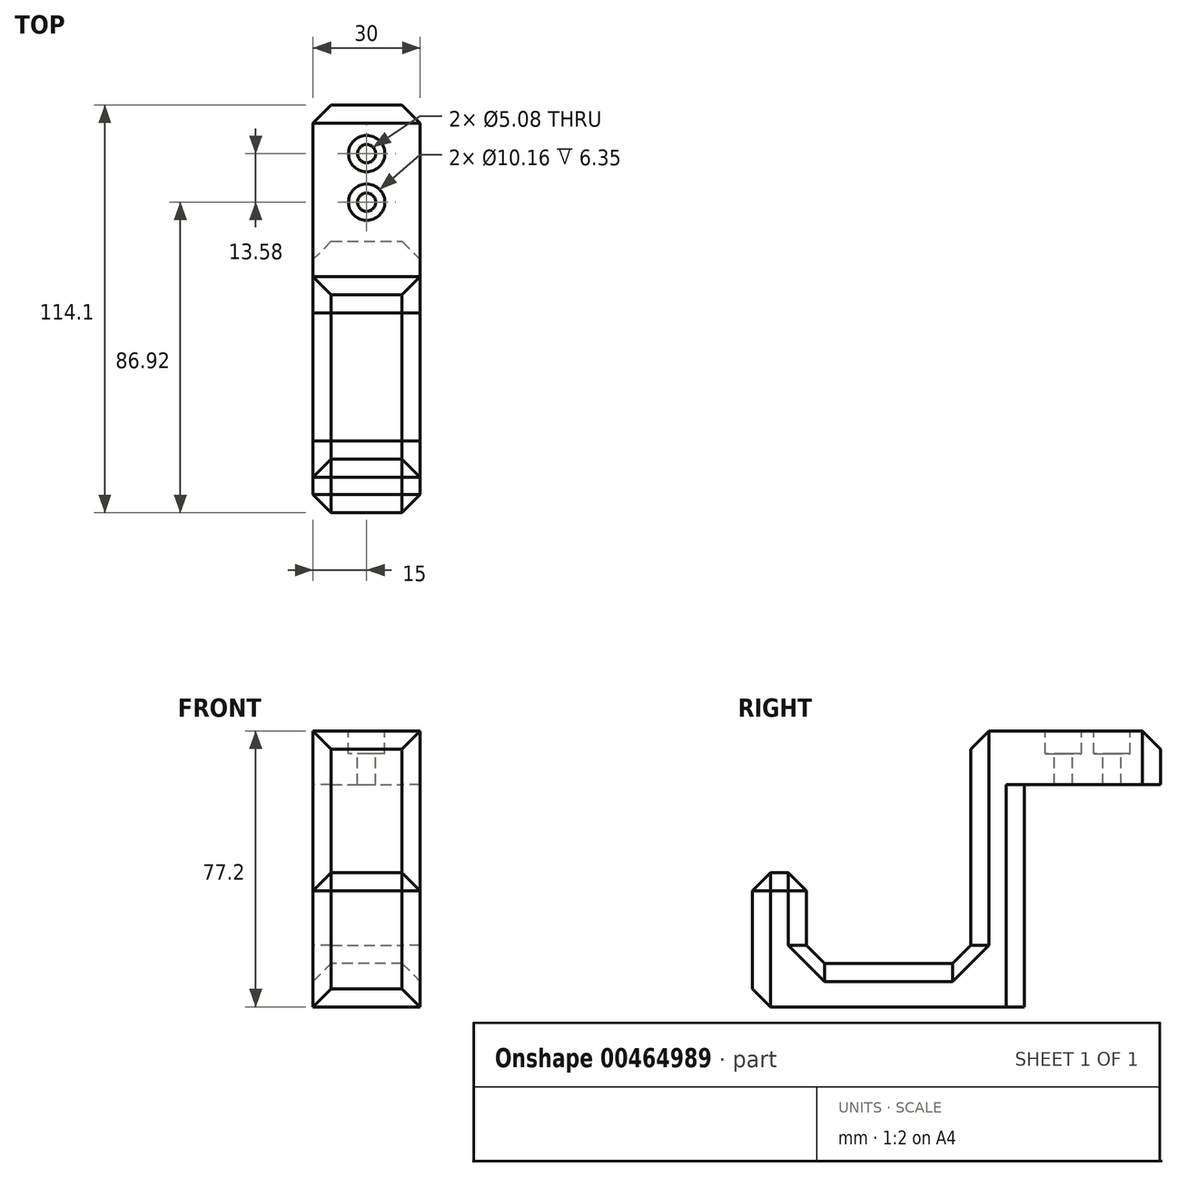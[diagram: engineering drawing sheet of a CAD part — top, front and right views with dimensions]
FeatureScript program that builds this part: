
annotation { "Feature Type Name" : "Feature", "Feature Type Description" : "" }
export const myFeature = defineFeature(function(context is Context, id is Id, definition is map)
    precondition{}
    {
        {
            var Q0;
            Q0=qCreatedBy(makeId("Front.planeOp"),FACE);
            var sketch = newSketch(context, id + "F0", { "sketchPlane" : qUnion([Q0])});
            skLineSegment(sketch, "E0.bottom", {"start": v(-36.48, 43.36) * mm, "end": v(-6.48, 43.36) * mm});
            skLineSegment(sketch, "E0.top", {"start": v(-36.48, -6.64) * mm, "end": v(-6.48, -6.64) * mm});
            skLineSegment(sketch, "E0.left", {"start": v(-36.48, 43.36) * mm, "end": v(-36.48, -6.64) * mm});
            skLineSegment(sketch, "E0.right", {"start": v(-6.48, 43.36) * mm, "end": v(-6.48, -6.64) * mm});
            skLineSegment(sketch, "E1.top", {"start": v(-36.48, 58.36) * mm, "end": v(-6.48, 58.36) * mm});
            skLineSegment(sketch, "E1.left", {"start": v(-36.48, 43.36) * mm, "end": v(-36.48, 58.36) * mm});
            skLineSegment(sketch, "E1.right", {"start": v(-6.48, 43.36) * mm, "end": v(-6.48, 58.36) * mm});
            skLineSegment(sketch, "E2.top", {"start": v(-36.48, -32.04) * mm, "end": v(-6.48, -32.04) * mm});
            skLineSegment(sketch, "E2.left", {"start": v(-36.48, -6.64) * mm, "end": v(-36.48, -32.04) * mm});
            skLineSegment(sketch, "E2.right", {"start": v(-6.48, -6.64) * mm, "end": v(-6.48, -32.04) * mm});
            skSolve(sketch);
        }
        {
            var Q0;
            Q0=makeQuery(id+"F0.imprint","IMPRINT",FACE,{"disambiguationData":[TD([[makeQuery(id+"F0.imprint","IMPRINT",EDGE,{"derivedFrom":sQuery(id+"F0.wireOp",EDGE,"E0.bottom")}),1.0]])]});
            var Q1;
            Q1=makeQuery(id+"F0.imprint","IMPRINT",FACE,{"disambiguationData":[TD([[makeQuery(id+"F0.imprint","IMPRINT",EDGE,{"derivedFrom":sQuery(id+"F0.wireOp",EDGE,"E0.left")}),1.0]])]});
            var Q2;
            Q2=makeQuery(id+"F0.imprint","IMPRINT",FACE,{"disambiguationData":[TD([[makeQuery(id+"F0.imprint","IMPRINT",EDGE,{"derivedFrom":sQuery(id+"F0.wireOp",EDGE,"E0.top")}),-1.0]])]});
            extrude(context, id + "F1", {"entities" : qUnion([Q0, Q1, Q2]), "depth" : 15 * mm});
        }
        {
            var Q0;
            Q0=makeQuery(id+"F0.imprint","IMPRINT",FACE,{"disambiguationData":[TD([[makeQuery(id+"F0.imprint","IMPRINT",EDGE,{"derivedFrom":sQuery(id+"F0.wireOp",EDGE,"E0.bottom")}),1.0]])]});
            extrude(context, id + "F2", {"entities" : qUnion([Q0]), "operationType" : NewBodyOperationType.ADD, "oppositeDirection" : true, "depth" : 38.1 * mm});
        }
        {
            var Q0;
            {var subQ0=sQuery(id+"F0.wireOp",EDGE,"E1.left");Q0=makeQuery(id+"F2.boolean.opBoolean","MERGE",FACE,{"derivedFrom":[makeQuery(id+"F1.opExtrude","SWEPT_FACE",FACE,{"disambiguationData":[OSD([sQuery(id+"F0.wireOp",EDGE,"E0.left"),subQ0,sQuery(id+"F0.wireOp",EDGE,"E2.left")])]}),makeQuery(id+"F2.opExtrude","SWEPT_FACE",FACE,{"disambiguationData":[OSD([subQ0])]})]});}
            var sketch = newSketch(context, id + "F3", { "sketchPlane" : qUnion([Q0])});
            skLineSegment(sketch, "E3.bottom", {"start": v(-38.1, 58.36) * mm, "end": v(0, 58.36) * mm});
            skLineSegment(sketch, "E3.top", {"start": v(-38.1, 43.36) * mm, "end": v(0, 43.36) * mm});
            skLineSegment(sketch, "E3.left", {"start": v(-38.1, 58.36) * mm, "end": v(-38.1, 43.36) * mm});
            skLineSegment(sketch, "E3.right", {"start": v(0, 58.36) * mm, "end": v(0, 43.36) * mm});
            skSolve(sketch);
        }
        {
            var Q0;
            Q0=makeQuery(id+"F3.imprint","IMPRINT",FACE,{"disambiguationData":[TD([[makeQuery(id+"F3.imprint","IMPRINT",EDGE,{"derivedFrom":sQuery(id+"F3.wireOp",EDGE,"E3.bottom")}),1.0]])]});
            var Q1;
            Q1=sQuery(id+"F3.wireOp",EDGE,"E3.right");
            revolve(context, id + "F4", {"operationType" : NewBodyOperationType.ADD, "entities" : qUnion([Q0]), "axis" : qUnion([Q1]), "revolveType" : RevolveType.ONE_DIRECTION, "oppositeDirection" : true, "angle" : 60 * degree});
        }
        {
            var Q0;
            {var subQ0=sQuery(id+"F0.wireOp",EDGE,"E1.right");Q0=makeQuery(id+"F2.boolean.opBoolean","MERGE",FACE,{"derivedFrom":[makeQuery(id+"F1.opExtrude","SWEPT_FACE",FACE,{"disambiguationData":[OSD([sQuery(id+"F0.wireOp",EDGE,"E0.right"),subQ0,sQuery(id+"F0.wireOp",EDGE,"E2.right")])]}),makeQuery(id+"F2.opExtrude","SWEPT_FACE",FACE,{"disambiguationData":[OSD([subQ0])]})]});}
            var sketch = newSketch(context, id + "F5", { "sketchPlane" : qUnion([Q0])});
            skLineSegment(sketch, "E4.bottom", {"start": v(0, 43.36) * mm, "end": v(38.1, 43.36) * mm});
            skLineSegment(sketch, "E4.top", {"start": v(0, 58.36) * mm, "end": v(38.1, 58.36) * mm});
            skLineSegment(sketch, "E4.left", {"start": v(0, 43.36) * mm, "end": v(0, 58.36) * mm});
            skLineSegment(sketch, "E4.right", {"start": v(38.1, 43.36) * mm, "end": v(38.1, 58.36) * mm});
            skSolve(sketch);
        }
        {
            var Q0;
            Q0=makeQuery(id+"F5.imprint","IMPRINT",FACE,{"disambiguationData":[TD([[makeQuery(id+"F5.imprint","IMPRINT",EDGE,{"derivedFrom":sQuery(id+"F5.wireOp",EDGE,"E4.bottom")}),-1.0]])]});
            var Q1;
            Q1=sQuery(id+"F5.wireOp",EDGE,"E4.left");
            revolve(context, id + "F6", {"operationType" : NewBodyOperationType.ADD, "entities" : qUnion([Q0]), "axis" : qUnion([Q1]), "revolveType" : RevolveType.ONE_DIRECTION, "oppositeDirection" : true, "angle" : 60 * degree});
        }
        {
            var Q0;
            Q0=makeQuery(id+"F0.imprint","IMPRINT",FACE,{"disambiguationData":[TD([[makeQuery(id+"F0.imprint","IMPRINT",EDGE,{"derivedFrom":sQuery(id+"F0.wireOp",EDGE,"E0.top")}),-1.0]])]});
            extrude(context, id + "F7", {"entities" : qUnion([Q0]), "operationType" : NewBodyOperationType.ADD, "depth" : 61 * mm});
        }
        {
            var Q0;
            Q0=makeQuery(id+"F7.opExtrude","CAP_FACE",FACE,{"disambiguationData":[OSD([sQuery(id+"F0.wireOp",EDGE,"E0.top"),sQuery(id+"F0.wireOp",EDGE,"E2.top"),sQuery(id+"F0.wireOp",EDGE,"E2.left"),sQuery(id+"F0.wireOp",EDGE,"E2.right")])],"isStart":false});
            extrude(context, id + "F8", {"entities" : qUnion([Q0]), "operationType" : NewBodyOperationType.ADD, "depth" : 15 * mm});
        }
        {
            var Q0;
            {var subQ0=sQuery(id+"F0.wireOp",EDGE,"E0.top");Q0=makeQuery(id+"F8.boolean.opBoolean","MERGE",FACE,{"derivedFrom":[makeQuery(id+"F7.opExtrude","SWEPT_FACE",FACE,{"disambiguationData":[OSD([subQ0])]}),makeQuery(id+"F8.opExtrude","SWEPT_FACE",FACE,{"disambiguationData":[OSD([subQ0])]})]});}
            var sketch = newSketch(context, id + "F9", { "sketchPlane" : qUnion([Q0])});
            skLineSegment(sketch, "E5.bottom", {"start": v(-36.48, -76) * mm, "end": v(-6.48, -76) * mm});
            skLineSegment(sketch, "E5.top", {"start": v(-36.48, -61) * mm, "end": v(-6.48, -61) * mm});
            skLineSegment(sketch, "E5.left", {"start": v(-36.48, -76) * mm, "end": v(-36.48, -61) * mm});
            skLineSegment(sketch, "E5.right", {"start": v(-6.48, -76) * mm, "end": v(-6.48, -61) * mm});
            skSolve(sketch);
        }
        {
            var Q0;
            Q0=makeQuery(id+"F9.imprint","IMPRINT",FACE,{"disambiguationData":[TD([[makeQuery(id+"F9.imprint","IMPRINT",EDGE,{"derivedFrom":sQuery(id+"F9.wireOp",EDGE,"E5.bottom")}),1.0]])]});
            extrude(context, id + "F10", {"entities" : qUnion([Q0]), "operationType" : NewBodyOperationType.ADD, "depth" : 25.4 * mm});
        }
        {
            var Q0;
            {var subQ0=sQuery(id+"F0.wireOp",EDGE,"E1.top");Q0=makeQuery(id+"F6.boolean.opBoolean","MERGE",FACE,{"derivedFrom":[makeQuery(id+"F4.boolean.opBoolean","MERGE",FACE,{"derivedFrom":[makeQuery(id+"F2.boolean.opBoolean","MERGE",FACE,{"derivedFrom":[makeQuery(id+"F1.opExtrude","SWEPT_FACE",FACE,{"disambiguationData":[OSD([subQ0])]}),makeQuery(id+"F2.opExtrude","SWEPT_FACE",FACE,{"disambiguationData":[OSD([subQ0])]})]}),makeQuery(id+"F4.opRevolve","SWEPT_FACE",FACE,{"disambiguationData":[OSD([sQuery(id+"F3.wireOp",EDGE,"E3.bottom")])]})]}),makeQuery(id+"F6.opRevolve","SWEPT_FACE",FACE,{"disambiguationData":[OSD([sQuery(id+"F5.wireOp",EDGE,"E4.top")])]})]});}
            var sketch = newSketch(context, id + "F11", { "sketchPlane" : qUnion([Q0])});
            skLineSegment(sketch, "E6.bottom", {"start": v(-6.48, 0) * mm, "end": v(33.21, 0) * mm});
            skLineSegment(sketch, "E6.top", {"start": v(-6.48, 45.82) * mm, "end": v(33.21, 45.82) * mm});
            skLineSegment(sketch, "E6.left", {"start": v(-6.48, 0) * mm, "end": v(-6.48, 45.82) * mm});
            skLineSegment(sketch, "E6.right", {"start": v(33.21, 0) * mm, "end": v(33.21, 45.82) * mm});
            skLineSegment(sketch, "E7.bottom", {"start": v(-36.48, 0) * mm, "end": v(-73.03, 0) * mm});
            skLineSegment(sketch, "E7.top", {"start": v(-36.48, 44.07) * mm, "end": v(-73.03, 44.07) * mm});
            skLineSegment(sketch, "E7.left", {"start": v(-36.48, 0) * mm, "end": v(-36.48, 44.07) * mm});
            skLineSegment(sketch, "E7.right", {"start": v(-73.03, 0) * mm, "end": v(-73.03, 44.07) * mm});
            skSolve(sketch);
        }
        {
            var Q0;
            {var subQ1=sQuery(id+"F3.wireOp",EDGE,"E3.bottom");var subQ2=makeQuery(id+"F4.opRevolve","SWEPT_EDGE",EDGE,{"disambiguationData":[OSD([subQ1,sQuery(id+"F3.wireOp",EDGE,"E3.left")])]});Q0=makeQuery(id+"F11.imprint","IMPRINT",FACE,{"disambiguationData":[TD([[makeQuery(id+"F11.imprint","IMPRINT",EDGE,{"derivedFrom":subQ2}),-1.0]])]});}
            var Q1;
            {var subQ1=sQuery(id+"F5.wireOp",EDGE,"E4.top");var subQ2=makeQuery(id+"F6.opRevolve","SWEPT_EDGE",EDGE,{"disambiguationData":[OSD([subQ1,sQuery(id+"F5.wireOp",EDGE,"E4.right")])]});Q1=makeQuery(id+"F11.imprint","IMPRINT",FACE,{"disambiguationData":[TD([[makeQuery(id+"F11.imprint","IMPRINT",EDGE,{"derivedFrom":subQ2}),1.0]])]});}
            extrude(context, id + "F12", {"entities" : qUnion([Q0, Q1]), "operationType" : NewBodyOperationType.REMOVE, "oppositeDirection" : true, "depth" : 26.92 * mm, "offsetDistance" : 25.4 * mm});
        }
        {
            var Q0;
            {var subQ0=sQuery(id+"F0.wireOp",EDGE,"E1.top");Q0=makeQuery(id+"F6.boolean.opBoolean","MERGE",FACE,{"derivedFrom":[makeQuery(id+"F4.boolean.opBoolean","MERGE",FACE,{"derivedFrom":[makeQuery(id+"F2.boolean.opBoolean","MERGE",FACE,{"derivedFrom":[makeQuery(id+"F1.opExtrude","SWEPT_FACE",FACE,{"disambiguationData":[OSD([subQ0])]}),makeQuery(id+"F2.opExtrude","SWEPT_FACE",FACE,{"disambiguationData":[OSD([subQ0])]})]}),makeQuery(id+"F4.opRevolve","SWEPT_FACE",FACE,{"disambiguationData":[OSD([sQuery(id+"F3.wireOp",EDGE,"E3.bottom")])]})]}),makeQuery(id+"F6.opRevolve","SWEPT_FACE",FACE,{"disambiguationData":[OSD([sQuery(id+"F5.wireOp",EDGE,"E4.top")])]})]});}
            var sketch = newSketch(context, id + "F13", { "sketchPlane" : qUnion([Q0])});
            skLineSegment(sketch, "E8", {"start": v(-36.48, 38.1) * mm, "end": v(-6.48, 38.1) * mm});
            skLineSegment(sketch, "E9", {"start": v(-21.48, 38.1) * mm, "end": v(-21.48, 10.92) * mm});
            skLineSegment(sketch, "E10", {"start": v(-21.48, 24.5) * mm, "end": v(-15, 24.5) * mm});
            skSolve(sketch);
        }
        {
            var Q0;
            Q0=sQuery(id+"F13.wireOp",VERTEX,"E10.start");
            var Q1;
            Q1=makeQuery(id+"F1.opExtrude","SWEPT_BODY",BODY,{"disambiguationData":[OSD([sQuery(id+"F0.wireOp",EDGE,"E0.left"),sQuery(id+"F0.wireOp",EDGE,"E0.right"),sQuery(id+"F0.wireOp",EDGE,"E1.top"),sQuery(id+"F0.wireOp",EDGE,"E1.left"),sQuery(id+"F0.wireOp",EDGE,"E1.right"),sQuery(id+"F0.wireOp",EDGE,"E2.top"),sQuery(id+"F0.wireOp",EDGE,"E2.left"),sQuery(id+"F0.wireOp",EDGE,"E2.right")])]});
            hole(context, id + "F14", {"style" : HoleStyle.C_BORE, "endStyle" : HoleEndStyle.THROUGH, "holeDiameter" : 5.08 * mm, "cBoreDiameter" : 10.16 * mm, "cBoreDepth" : 6.35 * mm, "majorDiameter" : 6.35 * mm, "isTappedThrough" : true, "tappedDepth" : 12.7 * mm, "tapClearance" : 3, "locations" : qUnion([Q0]), "scope" : qUnion([Q1])});
        }
        {
            var Q0;
            Q0=sQuery(id+"F13.wireOp",VERTEX,"E9.end");
            var Q1;
            Q1=makeQuery(id+"F1.opExtrude","SWEPT_BODY",BODY,{"disambiguationData":[OSD([sQuery(id+"F0.wireOp",EDGE,"E0.left"),sQuery(id+"F0.wireOp",EDGE,"E0.right"),sQuery(id+"F0.wireOp",EDGE,"E1.top"),sQuery(id+"F0.wireOp",EDGE,"E1.left"),sQuery(id+"F0.wireOp",EDGE,"E1.right"),sQuery(id+"F0.wireOp",EDGE,"E2.top"),sQuery(id+"F0.wireOp",EDGE,"E2.left"),sQuery(id+"F0.wireOp",EDGE,"E2.right")])]});
            hole(context, id + "F15", {"style" : HoleStyle.C_BORE, "endStyle" : HoleEndStyle.THROUGH, "holeDiameter" : 5.08 * mm, "cBoreDiameter" : 10.16 * mm, "cBoreDepth" : 6.35 * mm, "majorDiameter" : 6.35 * mm, "isTappedThrough" : true, "tappedDepth" : 12.7 * mm, "tapClearance" : 3, "locations" : qUnion([Q0]), "scope" : qUnion([Q1])});
        }
        {
            var Q0;
            {var subQ0=sQuery(id+"F0.wireOp",EDGE,"E2.right");var subQ1=sQuery(id+"F0.wireOp",EDGE,"E1.right");Q0=makeQuery(id+"F12.boolean.opBoolean","MERGE",FACE,{"derivedFrom":[makeQuery(id+"F10.boolean.opBoolean","MERGE",FACE,{"derivedFrom":[makeQuery(id+"F8.boolean.opBoolean","MERGE",FACE,{"derivedFrom":[makeQuery(id+"F7.boolean.opBoolean","MERGE",FACE,{"derivedFrom":[makeQuery(id+"F2.boolean.opBoolean","MERGE",FACE,{"derivedFrom":[makeQuery(id+"F1.opExtrude","SWEPT_FACE",FACE,{"disambiguationData":[OSD([sQuery(id+"F0.wireOp",EDGE,"E0.right"),subQ1,subQ0])]}),makeQuery(id+"F2.opExtrude","SWEPT_FACE",FACE,{"disambiguationData":[OSD([subQ1])]})]}),makeQuery(id+"F7.opExtrude","SWEPT_FACE",FACE,{"disambiguationData":[OSD([subQ0])]})]}),makeQuery(id+"F8.opExtrude","SWEPT_FACE",FACE,{"disambiguationData":[OSD([subQ0])]})]}),makeQuery(id+"F10.opExtrude","SWEPT_FACE",FACE,{"disambiguationData":[OSD([sQuery(id+"F9.wireOp",EDGE,"E5.right")])]})]})],"fromTools":[makeQuery(id+"F12.opExtrude","SWEPT_FACE",FACE,{"disambiguationData":[OSD([sQuery(id+"F11.wireOp",EDGE,"E6.left")])]})]});}
            var sketch = newSketch(context, id + "F16", { "sketchPlane" : qUnion([Q0])});
            skLineSegment(sketch, "E11", {"start": v(-69.65, -18.84) * mm, "end": v(14.77, -18.84) * mm});
            skLineSegment(sketch, "E12", {"start": v(-69.65, -18.84) * mm, "end": v(-84.88, -18.84) * mm});
            skLineSegment(sketch, "E13.bottom", {"start": v(-82.04, -18.84) * mm, "end": v(13.44, -18.84) * mm});
            skLineSegment(sketch, "E13.top", {"start": v(-82.04, -58.56) * mm, "end": v(13.44, -58.56) * mm});
            skLineSegment(sketch, "E13.left", {"start": v(-82.04, -18.84) * mm, "end": v(-82.04, -58.56) * mm});
            skLineSegment(sketch, "E13.right", {"start": v(13.44, -18.84) * mm, "end": v(13.44, -58.56) * mm});
            skSolve(sketch);
        }
        {
            var Q0;
            Q0=makeQuery(id+"F16.imprint","IMPRINT",FACE,{"disambiguationData":[TD([[makeQuery(id+"F16.imprint","IMPRINT",EDGE,{"derivedFrom":sQuery(id+"F16.wireOp",EDGE,"E13.top")}),1.0]])]});
            var Q1;
            {var subQ1=sQuery(id+"F9.wireOp",EDGE,"E5.right");var subQ2=sQuery(id+"F0.wireOp",EDGE,"E2.right");var subQ3=sQuery(id+"F0.wireOp",EDGE,"E1.right");var subQ4=sQuery(id+"F0.wireOp",EDGE,"E0.right");var subQ5=makeQuery(id+"F10.boolean.opBoolean","MERGE",FACE,{"derivedFrom":[makeQuery(id+"F8.boolean.opBoolean","MERGE",FACE,{"derivedFrom":[makeQuery(id+"F7.boolean.opBoolean","MERGE",FACE,{"derivedFrom":[makeQuery(id+"F2.boolean.opBoolean","MERGE",FACE,{"derivedFrom":[makeQuery(id+"F1.opExtrude","SWEPT_FACE",FACE,{"disambiguationData":[OSD([subQ4,subQ3,subQ2])]}),makeQuery(id+"F2.opExtrude","SWEPT_FACE",FACE,{"disambiguationData":[OSD([subQ3])]})]}),makeQuery(id+"F7.opExtrude","SWEPT_FACE",FACE,{"disambiguationData":[OSD([subQ2])]})]}),makeQuery(id+"F8.opExtrude","SWEPT_FACE",FACE,{"disambiguationData":[OSD([subQ2])]})]}),makeQuery(id+"F10.opExtrude","SWEPT_FACE",FACE,{"disambiguationData":[OSD([subQ1])]})]});var subQ10=sQuery(id+"F0.wireOp",EDGE,"E2.top");var subQ11=makeQuery(id+"FaSJNswUkA1flgG_1.opFillet","BLEND_EDGE",EDGE,{"blendedFrom":[makeQuery(id+"F8.boolean.opBoolean","MERGE",EDGE,{"derivedFrom":[makeQuery(id+"F7.boolean.opBoolean","MERGE",EDGE,{"derivedFrom":[makeQuery(id+"F1.opExtrude","SWEPT_EDGE",EDGE,{"disambiguationData":[OSD([subQ10,subQ2])]}),makeQuery(id+"F7.opExtrude","SWEPT_EDGE",EDGE,{"disambiguationData":[OSD([subQ10,subQ2])]})]}),makeQuery(id+"F8.opExtrude","SWEPT_EDGE",EDGE,{"disambiguationData":[OSD([subQ10,subQ2])]})]}),subQ5],"blendedInto":[subQ5]});Q1=makeQuery(id+"F16.imprint","IMPRINT",FACE,{"disambiguationData":[TD([[makeQuery(id+"F16.imprint","IMPRINT",EDGE,{"derivedFrom":subQ11}),1.0]])]});}
            extrude(context, id + "F17", {"entities" : qUnion([Q0, Q1]), "operationType" : NewBodyOperationType.REMOVE, "oppositeDirection" : true, "depth" : 60.96 * mm, "offsetDistance" : 25.4 * mm});
        }
        {
            var Q0;
            Q0=makeQuery(id+"F16.imprint","IMPRINT",FACE,{"disambiguationData":[TD([[makeQuery(id+"F16.imprint","IMPRINT",EDGE,{"derivedFrom":sQuery(id+"F16.wireOp",EDGE,"E13.top")}),1.0]])]});
            var Q1;
            {var subQ1=sQuery(id+"F0.wireOp",EDGE,"E2.right");var subQ6=sQuery(id+"F0.wireOp",EDGE,"E2.top");var subQ7=makeQuery(id+"F8.boolean.opBoolean","MERGE",EDGE,{"derivedFrom":[makeQuery(id+"F7.boolean.opBoolean","MERGE",EDGE,{"derivedFrom":[makeQuery(id+"F1.opExtrude","SWEPT_EDGE",EDGE,{"disambiguationData":[OSD([subQ6,subQ1])]}),makeQuery(id+"F7.opExtrude","SWEPT_EDGE",EDGE,{"disambiguationData":[OSD([subQ6,subQ1])]})]}),makeQuery(id+"F8.opExtrude","SWEPT_EDGE",EDGE,{"disambiguationData":[OSD([subQ6,subQ1])]})]});Q1=makeQuery(id+"F16.imprint","IMPRINT",FACE,{"disambiguationData":[TD([[makeQuery(id+"F16.imprint","IMPRINT",EDGE,{"derivedFrom":subQ7}),1.0]])]});}
            extrude(context, id + "F18", {"entities" : qUnion([Q0, Q1]), "operationType" : NewBodyOperationType.REMOVE, "oppositeDirection" : true, "depth" : 45.2 * mm, "offsetDistance" : 25.4 * mm});
        }
        {
            var Q0;
            {var subQ0=sQuery(id+"F0.wireOp",EDGE,"E2.right");var subQ1=sQuery(id+"F0.wireOp",EDGE,"E0.top");var subQ2=sQuery(id+"F0.wireOp",EDGE,"E0.right");Q0=makeQuery(id+"F8.boolean.opBoolean","MERGE",EDGE,{"derivedFrom":[makeQuery(id+"F7.opExtrude","SWEPT_EDGE",EDGE,{"disambiguationData":[OSD([subQ2,subQ1,subQ0])]}),makeQuery(id+"F8.opExtrude","SWEPT_EDGE",EDGE,{"disambiguationData":[OSD([subQ2,subQ1,subQ0])]})]});}
            var Q1;
            {var subQ0=sQuery(id+"F0.wireOp",EDGE,"E2.left");var subQ1=sQuery(id+"F0.wireOp",EDGE,"E0.top");var subQ2=sQuery(id+"F0.wireOp",EDGE,"E0.left");Q1=makeQuery(id+"F8.boolean.opBoolean","MERGE",EDGE,{"derivedFrom":[makeQuery(id+"F7.opExtrude","SWEPT_EDGE",EDGE,{"disambiguationData":[OSD([subQ2,subQ1,subQ0])]}),makeQuery(id+"F8.opExtrude","SWEPT_EDGE",EDGE,{"disambiguationData":[OSD([subQ2,subQ1,subQ0])]})]});}
            var Q2;
            Q2=makeQuery(id+"F10.opExtrude","CAP_FACE",FACE,{"disambiguationData":[OSD([sQuery(id+"F9.wireOp",EDGE,"E5.bottom"),sQuery(id+"F9.wireOp",EDGE,"E5.top"),sQuery(id+"F9.wireOp",EDGE,"E5.left"),sQuery(id+"F9.wireOp",EDGE,"E5.right")])],"isStart":false});
            var Q3;
            Q3=makeQuery(id+"F10.boolean.opBoolean","MERGE",FACE,{"derivedFrom":[makeQuery(id+"F8.opExtrude","CAP_FACE",FACE,{"disambiguationData":[OSD([sQuery(id+"F0.wireOp",EDGE,"E0.top"),sQuery(id+"F0.wireOp",EDGE,"E2.top"),sQuery(id+"F0.wireOp",EDGE,"E2.left"),sQuery(id+"F0.wireOp",EDGE,"E2.right")])],"isStart":false}),makeQuery(id+"F10.opExtrude","SWEPT_FACE",FACE,{"disambiguationData":[OSD([sQuery(id+"F9.wireOp",EDGE,"E5.bottom")])]})]});
            var Q4;
            Q4=makeQuery(id+"F18.boolean.opBoolean","COPY",FACE,{"derivedFrom":makeQuery(id+"F18.opExtrude","SWEPT_FACE",FACE,{"disambiguationData":[OSD([sQuery(id+"F16.wireOp",EDGE,"E13.bottom")])]})});
            var Q5;
            Q5=makeQuery(id+"F1.opExtrude","CAP_FACE",FACE,{"disambiguationData":[OSD([sQuery(id+"F0.wireOp",EDGE,"E0.left"),sQuery(id+"F0.wireOp",EDGE,"E0.right"),sQuery(id+"F0.wireOp",EDGE,"E1.top"),sQuery(id+"F0.wireOp",EDGE,"E1.left"),sQuery(id+"F0.wireOp",EDGE,"E1.right"),sQuery(id+"F0.wireOp",EDGE,"E2.top"),sQuery(id+"F0.wireOp",EDGE,"E2.left"),sQuery(id+"F0.wireOp",EDGE,"E2.right")])],"isStart":false});
            var Q6;
            Q6=makeQuery(id+"F10.opExtrude","SWEPT_FACE",FACE,{"disambiguationData":[OSD([sQuery(id+"F9.wireOp",EDGE,"E5.top")])]});
            var Q7;
            {var subQ0=sQuery(id+"F0.wireOp",EDGE,"E1.right");var subQ1=sQuery(id+"F0.wireOp",EDGE,"E1.top");Q7=makeQuery(id+"F12.boolean.opBoolean","MERGE",EDGE,{"derivedFrom":[makeQuery(id+"F2.boolean.opBoolean","MERGE",EDGE,{"derivedFrom":[makeQuery(id+"F1.opExtrude","SWEPT_EDGE",EDGE,{"disambiguationData":[OSD([subQ1,subQ0])]}),makeQuery(id+"F2.opExtrude","SWEPT_EDGE",EDGE,{"disambiguationData":[OSD([subQ1,subQ0])]})]})],"fromTools":[makeQuery(id+"F12.opExtrude","CAP_EDGE",EDGE,{"disambiguationData":[OSD([sQuery(id+"F11.wireOp",EDGE,"E6.left")])],"isStart":true})]});}
            var Q8;
            {var subQ0=sQuery(id+"F0.wireOp",EDGE,"E1.left");var subQ1=sQuery(id+"F0.wireOp",EDGE,"E1.top");Q8=makeQuery(id+"F12.boolean.opBoolean","MERGE",EDGE,{"derivedFrom":[makeQuery(id+"F2.boolean.opBoolean","MERGE",EDGE,{"derivedFrom":[makeQuery(id+"F1.opExtrude","SWEPT_EDGE",EDGE,{"disambiguationData":[OSD([subQ1,subQ0])]}),makeQuery(id+"F2.opExtrude","SWEPT_EDGE",EDGE,{"disambiguationData":[OSD([subQ1,subQ0])]})]})],"fromTools":[makeQuery(id+"F12.opExtrude","CAP_EDGE",EDGE,{"disambiguationData":[OSD([sQuery(id+"F11.wireOp",EDGE,"E7.left")])],"isStart":true})]});}
            var Q9;
            Q9=makeQuery(id+"F2.opExtrude","CAP_EDGE",EDGE,{"disambiguationData":[OSD([sQuery(id+"F0.wireOp",EDGE,"E1.top")])],"isStart":false});
            var Q10;
            Q10=makeQuery(id+"F1.opExtrude","CAP_EDGE",EDGE,{"disambiguationData":[OSD([sQuery(id+"F0.wireOp",EDGE,"E0.right"),sQuery(id+"F0.wireOp",EDGE,"E1.right"),sQuery(id+"F0.wireOp",EDGE,"E2.right")])],"isStart":true});
            var Q11;
            Q11=makeQuery(id+"F1.opExtrude","CAP_EDGE",EDGE,{"disambiguationData":[OSD([sQuery(id+"F0.wireOp",EDGE,"E0.left"),sQuery(id+"F0.wireOp",EDGE,"E1.left"),sQuery(id+"F0.wireOp",EDGE,"E2.left")])],"isStart":true});
            var Q12;
            {var subQ0=sQuery(id+"F5.wireOp",EDGE,"E4.right");Q12=makeQuery(id+"F12.boolean.opBoolean","MERGE",EDGE,{"derivedFrom":[makeQuery(id+"F6.boolean.opBoolean","MERGE",EDGE,{"derivedFrom":[makeQuery(id+"F2.opExtrude","CAP_EDGE",EDGE,{"disambiguationData":[OSD([sQuery(id+"F0.wireOp",EDGE,"E1.right")])],"isStart":false}),makeQuery(id+"F6.opRevolve","CAP_EDGE",EDGE,{"disambiguationData":[OSD([subQ0])],"isStart":true})]})],"fromTools":[makeQuery(id+"F12.opExtrude","SWEPT_EDGE",EDGE,{"disambiguationData":[OSD([sQuery(id+"F0.wireOp",EDGE,"E1.top"),sQuery(id+"F5.wireOp",EDGE,"E4.top"),subQ0,sQuery(id+"F11.wireOp",EDGE,"E6.left")])]})]});}
            var Q13;
            {var subQ0=sQuery(id+"F3.wireOp",EDGE,"E3.left");Q13=makeQuery(id+"F12.boolean.opBoolean","MERGE",EDGE,{"derivedFrom":[makeQuery(id+"F4.boolean.opBoolean","MERGE",EDGE,{"derivedFrom":[makeQuery(id+"F2.opExtrude","CAP_EDGE",EDGE,{"disambiguationData":[OSD([sQuery(id+"F0.wireOp",EDGE,"E1.left")])],"isStart":false}),makeQuery(id+"F4.opRevolve","CAP_EDGE",EDGE,{"disambiguationData":[OSD([subQ0])],"isStart":true})]})],"fromTools":[makeQuery(id+"F12.opExtrude","SWEPT_EDGE",EDGE,{"disambiguationData":[OSD([sQuery(id+"F0.wireOp",EDGE,"E1.top"),sQuery(id+"F3.wireOp",EDGE,"E3.bottom"),subQ0,sQuery(id+"F11.wireOp",EDGE,"E7.left")])]})]});}
            chamfer(context, id + "F19", {"entities" : qUnion([Q0, Q1, Q2, Q3, Q4, Q5, Q6, Q7, Q8, Q9, Q10, Q11, Q12, Q13]), "width" : 5.08 * mm, "tangentPropagation" : true});
        }
    });
